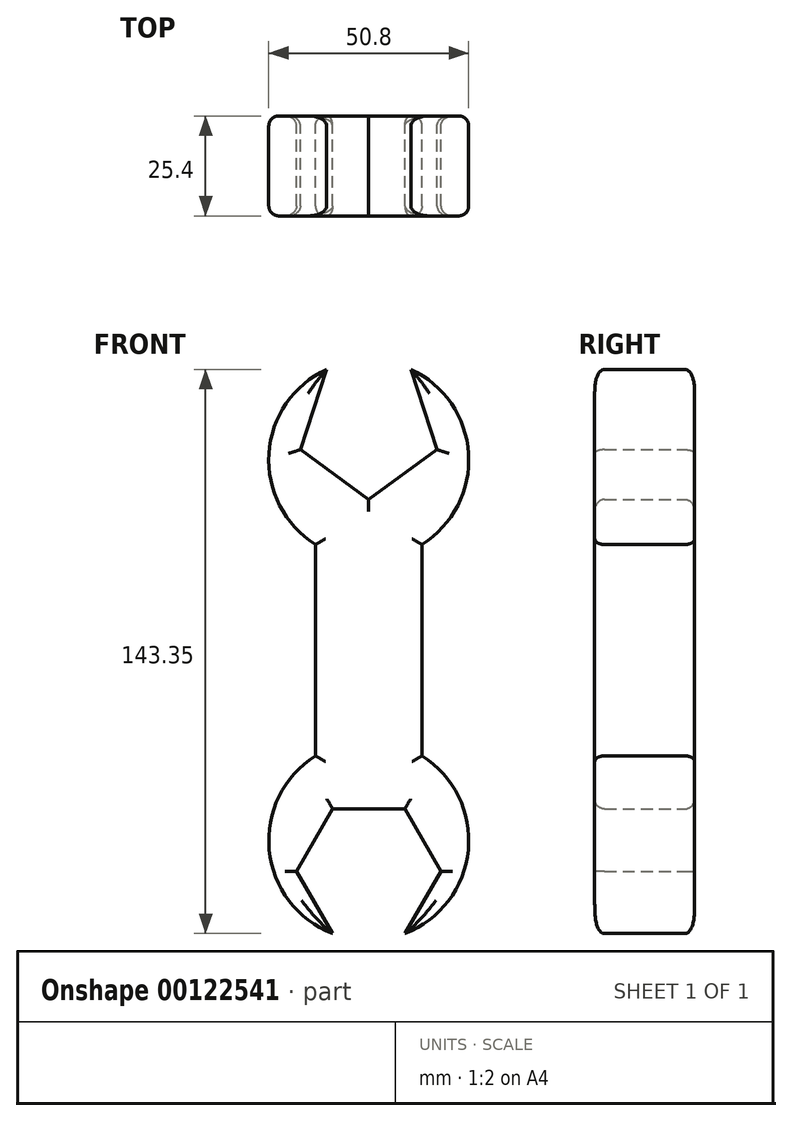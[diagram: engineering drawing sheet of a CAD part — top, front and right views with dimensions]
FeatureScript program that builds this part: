
annotation { "Feature Type Name" : "Feature", "Feature Type Description" : "" }
export const myFeature = defineFeature(function(context is Context, id is Id, definition is map)
    precondition{}
    {
        {
            var Q0;
            Q0=qCreatedBy(makeId("Front.planeOp"),FACE);
            var sketch = newSketch(context, id + "F0", { "sketchPlane" : qUnion([Q0])});
            skCircle(sketch, "E0", {"center": v(0, -38.95) * mm, "radius": 25.4 * mm});
            skLineSegment(sketch, "E1.left", {"start": v(-13.56, -17.47) * mm, "end": v(-13.56, 36.26) * mm});
            skLineSegment(sketch, "E1.right", {"start": v(13.56, -17.47) * mm, "end": v(13.56, 36.26) * mm});
            skCircle(sketch, "E2.cCircle", {"center": v(0, -46.83) * mm, "radius": 15.9 * mm, "construction": true});
            skLineSegment(sketch, "E2.0", {"start": v(-9.17, -30.94) * mm, "end": v(9.17, -30.94) * mm});
            skLineSegment(sketch, "E2.1", {"start": v(9.17, -30.94) * mm, "end": v(18.35, -46.83) * mm});
            skLineSegment(sketch, "E2.2", {"start": v(18.35, -46.83) * mm, "end": v(9.17, -62.72) * mm});
            skLineSegment(sketch, "E2.3", {"start": v(9.17, -62.72) * mm, "end": v(-9.17, -62.72) * mm});
            skLineSegment(sketch, "E2.4", {"start": v(-9.17, -62.72) * mm, "end": v(-18.35, -46.83) * mm});
            skLineSegment(sketch, "E2.5", {"start": v(-18.35, -46.83) * mm, "end": v(-9.17, -30.94) * mm});
            skPoint(sketch, "E2.0.midPoint", {"position": v(0, -30.94) * mm});
            skCircle(sketch, "E3", {"center": v(0, 57.72) * mm, "radius": 25.4 * mm});
            skCircle(sketch, "E4.cCircle", {"center": v(0, 65.98) * mm, "radius": 14.76 * mm, "construction": true});
            skLineSegment(sketch, "E4.0", {"start": v(17.36, 60.34) * mm, "end": v(0, 47.73) * mm});
            skLineSegment(sketch, "E4.1", {"start": v(0, 47.73) * mm, "end": v(-17.36, 60.34) * mm});
            skLineSegment(sketch, "E4.2", {"start": v(-17.36, 60.34) * mm, "end": v(-10.73, 80.74) * mm});
            skLineSegment(sketch, "E4.3", {"start": v(-10.73, 80.74) * mm, "end": v(10.73, 80.74) * mm});
            skLineSegment(sketch, "E4.4", {"start": v(10.73, 80.74) * mm, "end": v(17.36, 60.34) * mm});
            skPoint(sketch, "E4.0.midPoint", {"position": v(8.68, 54.03) * mm});
            skSolve(sketch);
        }
        {
            var Q0;
            {var subQ0=sQuery(id+"F0.wireOp",EDGE,"E1.left");var subQ1=sQuery(id+"F0.wireOp",EDGE,"E0");var subQ2=makeQuery(id+"F0.imprint","INTERSECT",VERTEX,{"derivedFrom":[subQ1,subQ0]});Q0=makeQuery(id+"F0.imprint","IMPRINT",FACE,{"disambiguationData":[TD([[makeQuery(id+"F0.imprint","IMPRINT",EDGE,{"disambiguationData":[TD([[subQ2,1.0]])],"derivedFrom":subQ1}),-1.0]])]});}
            var Q1;
            Q1=makeQuery(id+"F0.imprint","IMPRINT",FACE,{"disambiguationData":[TD([[makeQuery(id+"F0.imprint","IMPRINT",EDGE,{"derivedFrom":sQuery(id+"F0.wireOp",EDGE,"E4.0")}),1.0]])]});
            var Q2;
            Q2=makeQuery(id+"F0.imprint","IMPRINT",FACE,{"disambiguationData":[TD([[makeQuery(id+"F0.imprint","IMPRINT",EDGE,{"derivedFrom":sQuery(id+"F0.wireOp",EDGE,"E2.0")}),1.0]])]});
            extrude(context, id + "F1", {"entities" : qUnion([Q0, Q1, Q2]), "depth" : 25.4 * mm});
        }
        {
            var Q0;
            Q0=makeQuery(id+"F1.opExtrude","CAP_EDGE",EDGE,{"disambiguationData":[OSD([sQuery(id+"F0.wireOp",EDGE,"E2.5")])],"isStart":false});
            var Q1;
            Q1=makeQuery(id+"F1.opExtrude","CAP_EDGE",EDGE,{"disambiguationData":[OSD([sQuery(id+"F0.wireOp",EDGE,"E2.0")])],"isStart":false});
            var Q2;
            Q2=makeQuery(id+"F1.opExtrude","CAP_EDGE",EDGE,{"disambiguationData":[OSD([sQuery(id+"F0.wireOp",EDGE,"E2.1")])],"isStart":false});
            var Q3;
            Q3=makeQuery(id+"F1.opExtrude","CAP_EDGE",EDGE,{"disambiguationData":[OSD([sQuery(id+"F0.wireOp",EDGE,"E2.4")])],"isStart":false});
            var Q4;
            Q4=makeQuery(id+"F1.opExtrude","CAP_EDGE",EDGE,{"disambiguationData":[OSD([sQuery(id+"F0.wireOp",EDGE,"E2.2")])],"isStart":false});
            var Q5;
            {var subQ0=sQuery(id+"F0.wireOp",EDGE,"E0");Q5=makeQuery(id+"F1.opExtrude","CAP_EDGE",EDGE,{"disambiguationData":[OSD([subQ0]),TDD([makeQuery(id+"F0.imprint","IMPRINT",EDGE,{"disambiguationData":[TD([[makeQuery(id+"F0.imprint","INTERSECT",VERTEX,{"derivedFrom":[subQ0,sQuery(id+"F0.wireOp",EDGE,"E1.right")]}),1.0]])],"derivedFrom":subQ0})])],"isStart":false});}
            var Q6;
            {var subQ0=sQuery(id+"F0.wireOp",EDGE,"E0");Q6=makeQuery(id+"F1.opExtrude","CAP_EDGE",EDGE,{"disambiguationData":[OSD([subQ0]),TDD([makeQuery(id+"F0.imprint","IMPRINT",EDGE,{"disambiguationData":[TD([[makeQuery(id+"F0.imprint","INTERSECT",VERTEX,{"derivedFrom":[subQ0,sQuery(id+"F0.wireOp",EDGE,"E1.left")]}),-1.0]])],"derivedFrom":subQ0})])],"isStart":false});}
            var Q7;
            Q7=makeQuery(id+"F1.opExtrude","CAP_EDGE",EDGE,{"disambiguationData":[OSD([sQuery(id+"F0.wireOp",EDGE,"E1.left")])],"isStart":false});
            var Q8;
            {var subQ0=sQuery(id+"F0.wireOp",EDGE,"E3");Q8=makeQuery(id+"F1.opExtrude","CAP_EDGE",EDGE,{"disambiguationData":[OSD([subQ0]),TDD([makeQuery(id+"F0.imprint","IMPRINT",EDGE,{"disambiguationData":[TD([[makeQuery(id+"F0.imprint","INTERSECT",VERTEX,{"derivedFrom":[sQuery(id+"F0.wireOp",EDGE,"E1.left"),subQ0]}),1.0]])],"derivedFrom":subQ0})])],"isStart":false});}
            var Q9;
            Q9=makeQuery(id+"F1.opExtrude","CAP_EDGE",EDGE,{"disambiguationData":[OSD([sQuery(id+"F0.wireOp",EDGE,"E4.1")])],"isStart":false});
            var Q10;
            Q10=makeQuery(id+"F1.opExtrude","CAP_EDGE",EDGE,{"disambiguationData":[OSD([sQuery(id+"F0.wireOp",EDGE,"E4.2")])],"isStart":false});
            var Q11;
            Q11=makeQuery(id+"F1.opExtrude","CAP_EDGE",EDGE,{"disambiguationData":[OSD([sQuery(id+"F0.wireOp",EDGE,"E4.4")])],"isStart":false});
            var Q12;
            Q12=makeQuery(id+"F1.opExtrude","CAP_EDGE",EDGE,{"disambiguationData":[OSD([sQuery(id+"F0.wireOp",EDGE,"E4.0")])],"isStart":false});
            var Q13;
            {var subQ0=sQuery(id+"F0.wireOp",EDGE,"E3");Q13=makeQuery(id+"F1.opExtrude","CAP_EDGE",EDGE,{"disambiguationData":[OSD([subQ0]),TDD([makeQuery(id+"F0.imprint","IMPRINT",EDGE,{"disambiguationData":[TD([[makeQuery(id+"F0.imprint","INTERSECT",VERTEX,{"derivedFrom":[sQuery(id+"F0.wireOp",EDGE,"E1.right"),subQ0]}),-1.0]])],"derivedFrom":subQ0})])],"isStart":false});}
            var Q14;
            Q14=makeQuery(id+"F1.opExtrude","CAP_EDGE",EDGE,{"disambiguationData":[OSD([sQuery(id+"F0.wireOp",EDGE,"E1.right")])],"isStart":false});
            fillet(context, id + "F2", {"entities" : qUnion([Q0, Q1, Q2, Q3, Q4, Q5, Q6, Q7, Q8, Q9, Q10, Q11, Q12, Q13, Q14]), "radius" : 2.54 * mm, "tangentPropagation" : true, "allowEdgeOverflow" : false});
        }
        {
            var Q0;
            {var subQ0=sQuery(id+"F0.wireOp",EDGE,"E3");Q0=makeQuery(id+"F1.opExtrude","CAP_EDGE",EDGE,{"disambiguationData":[OSD([subQ0]),TDD([makeQuery(id+"F0.imprint","IMPRINT",EDGE,{"disambiguationData":[TD([[makeQuery(id+"F0.imprint","INTERSECT",VERTEX,{"derivedFrom":[sQuery(id+"F0.wireOp",EDGE,"E1.right"),subQ0]}),-1.0]])],"derivedFrom":subQ0})])],"isStart":true});}
            var Q1;
            Q1=makeQuery(id+"F1.opExtrude","CAP_EDGE",EDGE,{"disambiguationData":[OSD([sQuery(id+"F0.wireOp",EDGE,"E4.4")])],"isStart":true});
            var Q2;
            Q2=makeQuery(id+"F1.opExtrude","CAP_EDGE",EDGE,{"disambiguationData":[OSD([sQuery(id+"F0.wireOp",EDGE,"E4.0")])],"isStart":true});
            var Q3;
            Q3=makeQuery(id+"F1.opExtrude","CAP_EDGE",EDGE,{"disambiguationData":[OSD([sQuery(id+"F0.wireOp",EDGE,"E4.2")])],"isStart":true});
            var Q4;
            Q4=makeQuery(id+"F1.opExtrude","CAP_EDGE",EDGE,{"disambiguationData":[OSD([sQuery(id+"F0.wireOp",EDGE,"E4.1")])],"isStart":true});
            var Q5;
            {var subQ0=sQuery(id+"F0.wireOp",EDGE,"E3");Q5=makeQuery(id+"F1.opExtrude","CAP_EDGE",EDGE,{"disambiguationData":[OSD([subQ0]),TDD([makeQuery(id+"F0.imprint","IMPRINT",EDGE,{"disambiguationData":[TD([[makeQuery(id+"F0.imprint","INTERSECT",VERTEX,{"derivedFrom":[sQuery(id+"F0.wireOp",EDGE,"E1.left"),subQ0]}),1.0]])],"derivedFrom":subQ0})])],"isStart":true});}
            var Q6;
            Q6=makeQuery(id+"F1.opExtrude","CAP_EDGE",EDGE,{"disambiguationData":[OSD([sQuery(id+"F0.wireOp",EDGE,"E1.right")])],"isStart":true});
            var Q7;
            Q7=makeQuery(id+"F1.opExtrude","CAP_EDGE",EDGE,{"disambiguationData":[OSD([sQuery(id+"F0.wireOp",EDGE,"E1.left")])],"isStart":true});
            var Q8;
            {var subQ0=sQuery(id+"F0.wireOp",EDGE,"E0");Q8=makeQuery(id+"F1.opExtrude","CAP_EDGE",EDGE,{"disambiguationData":[OSD([subQ0]),TDD([makeQuery(id+"F0.imprint","IMPRINT",EDGE,{"disambiguationData":[TD([[makeQuery(id+"F0.imprint","INTERSECT",VERTEX,{"derivedFrom":[subQ0,sQuery(id+"F0.wireOp",EDGE,"E1.right")]}),1.0]])],"derivedFrom":subQ0})])],"isStart":true});}
            var Q9;
            Q9=makeQuery(id+"F1.opExtrude","CAP_EDGE",EDGE,{"disambiguationData":[OSD([sQuery(id+"F0.wireOp",EDGE,"E2.1")])],"isStart":true});
            var Q10;
            Q10=makeQuery(id+"F1.opExtrude","CAP_EDGE",EDGE,{"disambiguationData":[OSD([sQuery(id+"F0.wireOp",EDGE,"E2.2")])],"isStart":true});
            var Q11;
            Q11=makeQuery(id+"F1.opExtrude","CAP_EDGE",EDGE,{"disambiguationData":[OSD([sQuery(id+"F0.wireOp",EDGE,"E2.0")])],"isStart":true});
            var Q12;
            Q12=makeQuery(id+"F1.opExtrude","CAP_EDGE",EDGE,{"disambiguationData":[OSD([sQuery(id+"F0.wireOp",EDGE,"E2.5")])],"isStart":true});
            var Q13;
            {var subQ0=sQuery(id+"F0.wireOp",EDGE,"E0");Q13=makeQuery(id+"F1.opExtrude","CAP_EDGE",EDGE,{"disambiguationData":[OSD([subQ0]),TDD([makeQuery(id+"F0.imprint","IMPRINT",EDGE,{"disambiguationData":[TD([[makeQuery(id+"F0.imprint","INTERSECT",VERTEX,{"derivedFrom":[subQ0,sQuery(id+"F0.wireOp",EDGE,"E1.left")]}),-1.0]])],"derivedFrom":subQ0})])],"isStart":true});}
            var Q14;
            Q14=makeQuery(id+"F1.opExtrude","CAP_EDGE",EDGE,{"disambiguationData":[OSD([sQuery(id+"F0.wireOp",EDGE,"E2.4")])],"isStart":true});
            fillet(context, id + "F3", {"entities" : qUnion([Q0, Q1, Q2, Q3, Q4, Q5, Q6, Q7, Q8, Q9, Q10, Q11, Q12, Q13, Q14]), "radius" : 2.54 * mm, "tangentPropagation" : true, "allowEdgeOverflow" : false});
        }
    });
